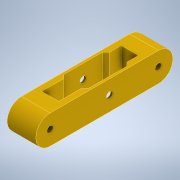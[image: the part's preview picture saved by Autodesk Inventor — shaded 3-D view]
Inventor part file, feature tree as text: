
AUTODESK INVENTOR PART (.ipt)
format: ipt  version: 2022 (Build 260153000, 153)  size: 213,504 bytes
history: native  units: mm
features: extrude x7, sketch x5, fillet x2, chamfer x1
ambient origin geometry x8: Origin, YZ Plane, XZ Plane, XY Plane, X Axis, Y Axis, Z Axis, Center Point
bodies: Solid1 (feature_tree)
feature tree (15):
  extrude  "Extrusion1"  Depth=10.0mm
  fillet  "Fillet1"  Radius=2.0mm
  extrude  "Extrusion2"  Depth=2.0mm
  extrude  "Extrusion3"  Depth=10.0mm TaperAngle=0.0deg
  extrude  "Extrusion4"  Depth=5.0mm
  extrude  "Extrusion5"  TaperAngle=0.0deg  [1 undecoded]
  extrude  "Extrusion6"  Depth=2.0mm
  extrude  "Extrusion7"  TaperAngle=0.0deg  [1 undecoded]
  fillet  "Fillet3"  Radius=12.0mm
  chamfer  "Chamfer2"  Distance=2.0mm
  sketch  "Sketch2"  dims[d0=60.0mm d1=10.0mm d2=2.0mm]
  sketch  "Sketch3"  dims[d3=2.0mm d4=2.0mm]
  sketch  "Sketch5"  dims[d5=2.0mm d6=10.0mm d7=0.0mm]
  sketch  "Sketch6"  dims[d8=10.0mm d9=5.0mm]
  sketch  "Sketch8"  dims[d10=2.2mm d11=0.0mm d12=0.0mm d13=20.678mm d14=0.0mm d15=0.0mm d17=12.0mm d18=2.0mm d19=2.0mm d20=10.0mm d21=0.0mm d22=10.0mm d23=10.0mm d24=0.0mm d27=0.0mm d28=0.0mm d29=8.0mm d30=8.0mm d31=16.0mm d32=7.0mm d33=10.0mm d34=0.0mm d50=0.25mm d51=0.25mm d53=2.2mm d55=5.0mm d56=1.25mm d57=2.0mm d58=45.0deg]
note: 2 required parameter values undecoded (feature->parameter linkage not recoverable at this tier; creation-order binding heuristic only, values carry confidence <= 0.55)
